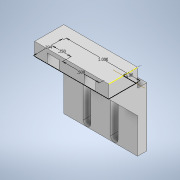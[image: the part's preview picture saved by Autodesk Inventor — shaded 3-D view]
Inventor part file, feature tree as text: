
AUTODESK INVENTOR PART (.ipt)
format: ipt  version: 2020 (Build 240168000, 168)  size: 202,240 bytes
history: native  units: in
note: dims shown in document units (in); Inventor stores cm internally (conversion verified against a paired STEP export)
features: sketch x6, extrude x5, hole x1, other x1
ambient origin geometry x8: Origin, YZ Plane, XZ Plane, XY Plane, X Axis, Y Axis, Z Axis, Center Point
bodies: Solid1 (feature_tree)
feature tree (13):
  sketch  "Sketch1"  dims[d0=1.0in d1=0.3937in]
  extrude  "Extrusion1"  Depth=0.3937in
  hole  "Hole1"  [1 undecoded]
  sketch  "Sketch2"  dims[d2=0.175in d3=0.0in d4=0.25in]
  sketch  "Sketch3"  dims[d5=0.5in]
  other  "Work Axis1"
  extrude  "Extrusion2"  Depth=0.025in
  extrude  "Extrusion3"  TaperAngle=45.0deg  [1 undecoded]
  extrude  "Extrusion4"  TaperAngle=45.0deg  [1 undecoded]
  extrude  "Extrusion5"  Depth=1.0in TaperAngle=0.0deg
  sketch  "Sketch4"  dims[d6=0.425in d7=0.75in d8=0.375in d9=0.25in d10=0.5635in d11=0.125in d12=0.0in d13=0.025in]
  sketch  "Sketch5"  dims[d14=0.025in d15=45.0deg]
  sketch  "Sketch6"  dims[d16=1.0in d17=0.0in d18=45.0deg d19=1.0in d20=0.0in d21=0.5in d22=0.125in d23=0.0in d24=0.185in d25=0.37in d26=0.1in d27=0.1in d28=0.8in d29=0.35in d30=0.1in d31=0.35in d32=0.1in d33=0.125in d34=0.0in]
note: 3 required parameter values undecoded (feature->parameter linkage not recoverable at this tier; creation-order binding heuristic only, values carry confidence <= 0.55)
